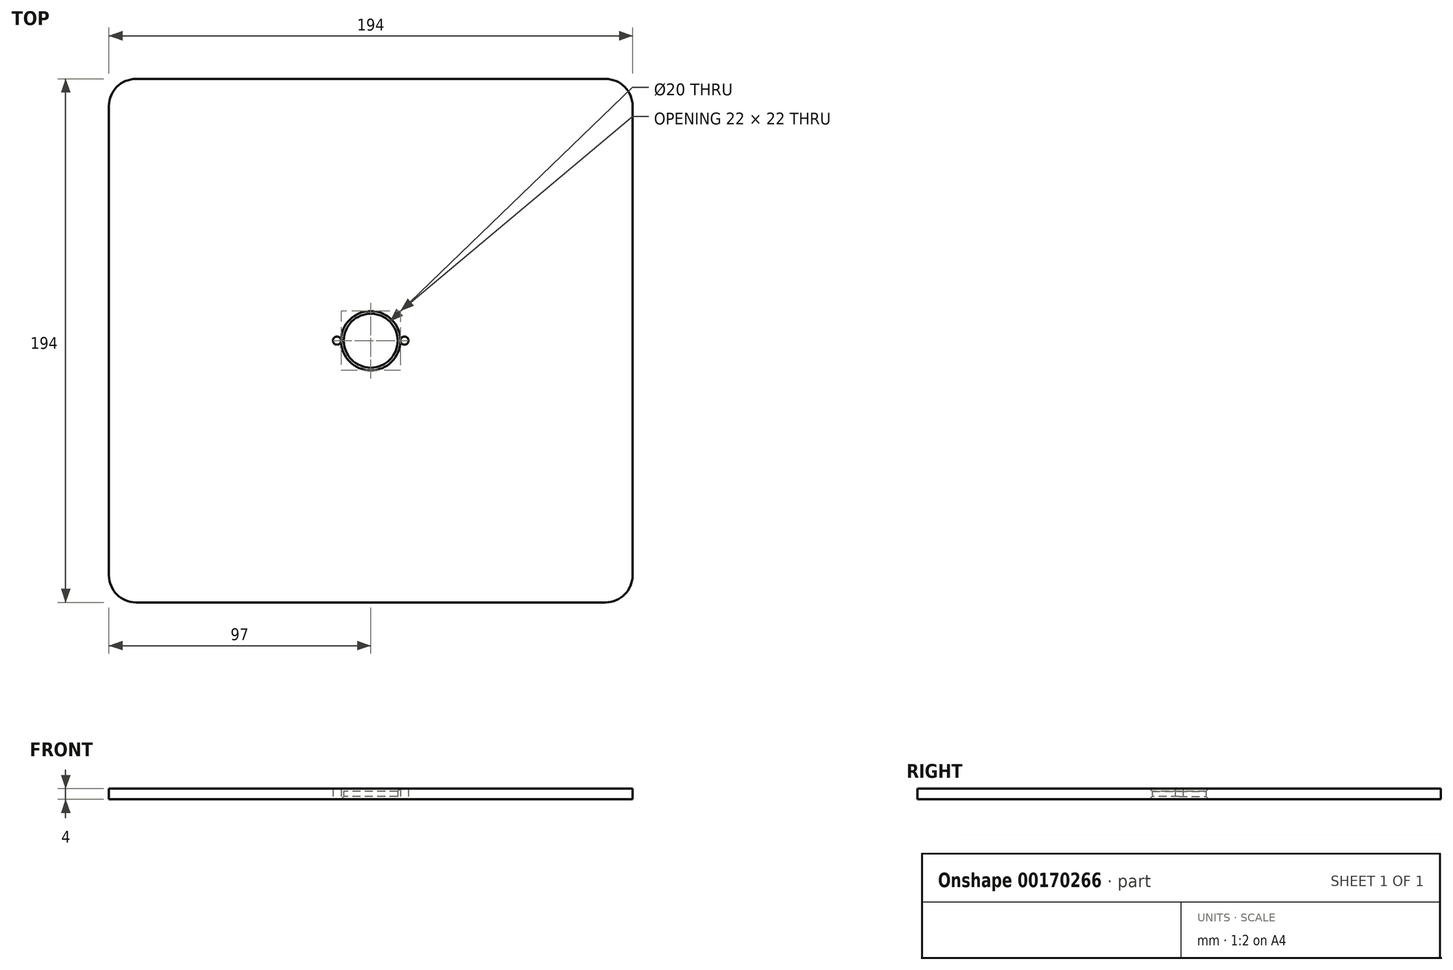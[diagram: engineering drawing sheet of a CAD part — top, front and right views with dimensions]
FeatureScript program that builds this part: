
annotation { "Feature Type Name" : "Feature", "Feature Type Description" : "" }
export const myFeature = defineFeature(function(context is Context, id is Id, definition is map)
    precondition{}
    {
        {
            var Q0;
            Q0=qCreatedBy(makeId("Top.planeOp"),FACE);
            var sketch = newSketch(context, id + "F0", { "sketchPlane" : qUnion([Q0])});
            skLineSegment(sketch, "E0.bottom", {"start": v(-97, 97) * mm, "end": v(97, 97) * mm});
            skLineSegment(sketch, "E0.top", {"start": v(-97, -97) * mm, "end": v(97, -97) * mm});
            skLineSegment(sketch, "E0.left", {"start": v(-97, 97) * mm, "end": v(-97, -97) * mm});
            skLineSegment(sketch, "E0.right", {"start": v(97, 97) * mm, "end": v(97, -97) * mm});
            skCircle(sketch, "E1", {"center": v(0, 0) * mm, "radius": 10 * mm});
            skCircle(sketch, "E2", {"center": v(12.5, 0) * mm, "radius": 1.5 * mm});
            skCircle(sketch, "E3", {"center": v(-12.5, 0) * mm, "radius": 1.5 * mm});
            skSolve(sketch);
        }
        {
            var Q0;
            Q0 = qSketchRegion(id + "F0", true);
            extrude(context, id + "F1", {"entities" : qUnion([Q0]), "depth" : 4 * mm});
        }
        {
            var Q0;
            Q0=makeQuery(id+"F1.opExtrude","CAP_EDGE",EDGE,{"disambiguationData":[OSD([sQuery(id+"F0.wireOp",EDGE,"E1")])],"isStart":false});
            var Q1;
            Q1=makeQuery(id+"F1.opExtrude","CAP_EDGE",EDGE,{"disambiguationData":[OSD([sQuery(id+"F0.wireOp",EDGE,"E1")])],"isStart":true});
            chamfer(context, id + "F2", {"entities" : qUnion([Q0, Q1]), "width" : 1 * mm, "tangentPropagation" : true});
        }
        {
            var Q0;
            Q0=makeQuery(id+"F1.opExtrude","SWEPT_EDGE",EDGE,{"disambiguationData":[OSD([sQuery(id+"F0.wireOp",EDGE,"E0.bottom"),sQuery(id+"F0.wireOp",EDGE,"E0.left")])]});
            var Q1;
            Q1=makeQuery(id+"F1.opExtrude","SWEPT_EDGE",EDGE,{"disambiguationData":[OSD([sQuery(id+"F0.wireOp",EDGE,"E0.top"),sQuery(id+"F0.wireOp",EDGE,"E0.left")])]});
            var Q2;
            Q2=makeQuery(id+"F1.opExtrude","SWEPT_EDGE",EDGE,{"disambiguationData":[OSD([sQuery(id+"F0.wireOp",EDGE,"E0.top"),sQuery(id+"F0.wireOp",EDGE,"E0.right")])]});
            var Q3;
            Q3=makeQuery(id+"F1.opExtrude","SWEPT_EDGE",EDGE,{"disambiguationData":[OSD([sQuery(id+"F0.wireOp",EDGE,"E0.bottom"),sQuery(id+"F0.wireOp",EDGE,"E0.right")])]});
            fillet(context, id + "F3", {"entities" : qUnion([Q0, Q1, Q2, Q3]), "radius" : 10 * mm, "tangentPropagation" : true, "allowEdgeOverflow" : false});
        }
    });
